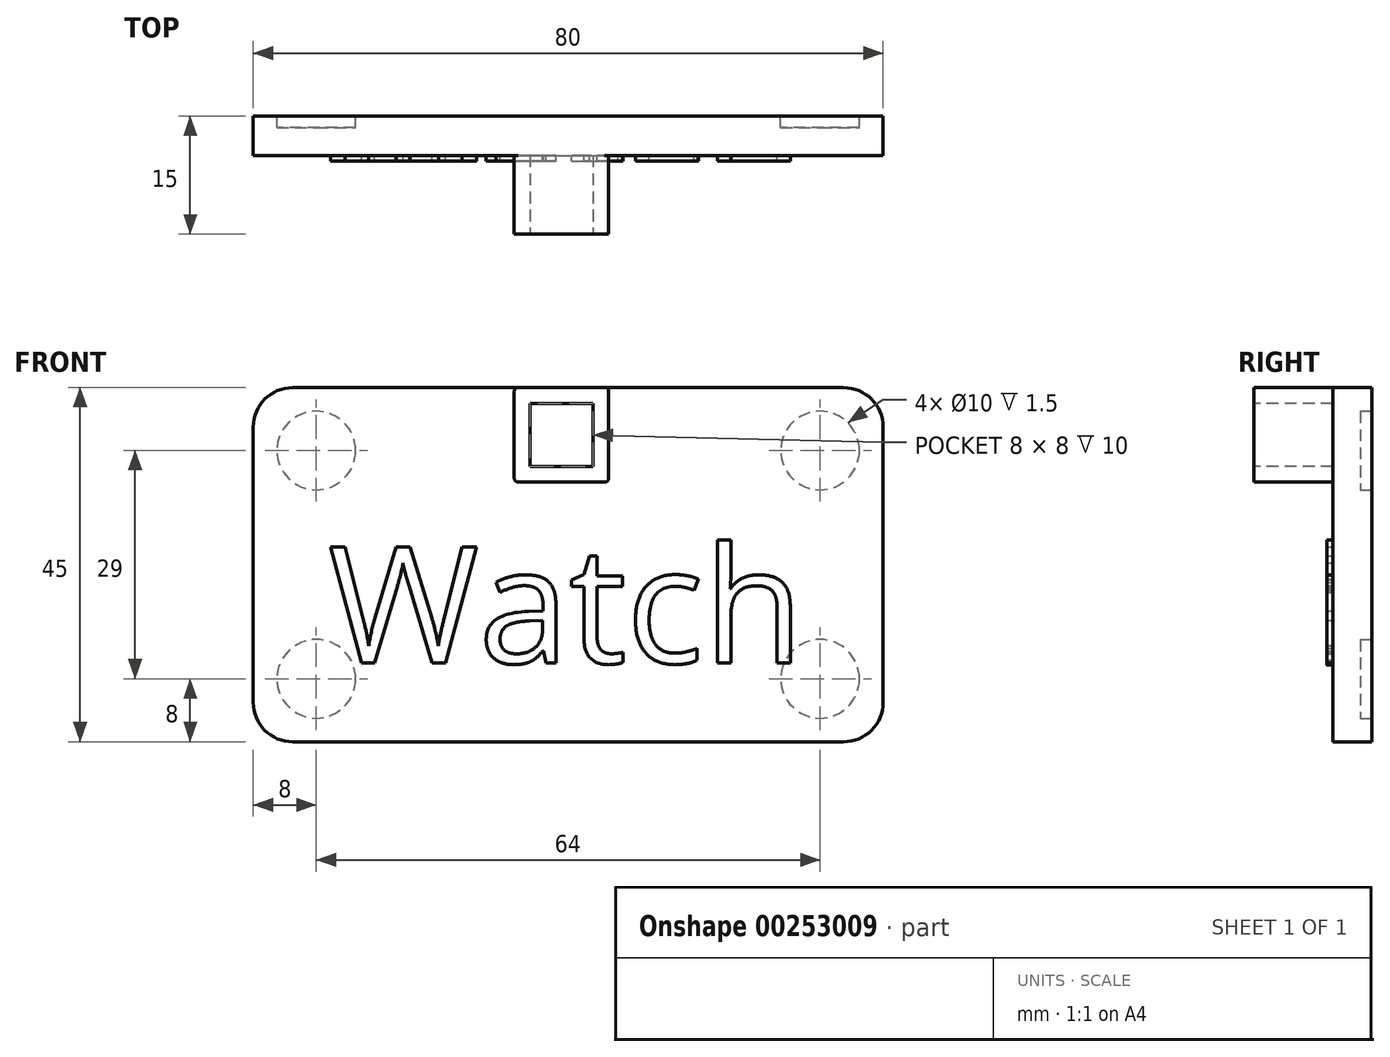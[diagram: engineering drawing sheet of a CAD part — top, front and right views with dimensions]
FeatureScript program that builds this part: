
annotation { "Feature Type Name" : "Feature", "Feature Type Description" : "" }
export const myFeature = defineFeature(function(context is Context, id is Id, definition is map)
    precondition{}
    {
        {
            var Q0;
            Q0=qCreatedBy(makeId("Front.planeOp"),FACE);
            var sketch = newSketch(context, id + "F0", { "sketchPlane" : qUnion([Q0])});
            skLineSegment(sketch, "E0.bottom", {"start": v(-40, 22.5) * mm, "end": v(40, 22.5) * mm});
            skLineSegment(sketch, "E0.top", {"start": v(-40, -22.5) * mm, "end": v(40, -22.5) * mm});
            skLineSegment(sketch, "E0.left", {"start": v(-40, 22.5) * mm, "end": v(-40, -22.5) * mm});
            skLineSegment(sketch, "E0.right", {"start": v(40, 22.5) * mm, "end": v(40, -22.5) * mm});
            skPoint(sketch, "E0.middle", {"position": v(0, 0) * mm});
            skSolve(sketch);
        }
        {
            var Q0;
            Q0 = qSketchRegion(id + "F0", true);
            extrude(context, id + "F1", {"entities" : qUnion([Q0]), "depth" : 5 * mm});
        }
        {
            var Q0;
            Q0=makeQuery(id+"F1.opExtrude","SWEPT_EDGE",EDGE,{"disambiguationData":[OSD([sQuery(id+"F0.wireOp",EDGE,"E0.bottom"),sQuery(id+"F0.wireOp",EDGE,"E0.right")])]});
            var Q1;
            Q1=makeQuery(id+"F1.opExtrude","SWEPT_EDGE",EDGE,{"disambiguationData":[OSD([sQuery(id+"F0.wireOp",EDGE,"E0.top"),sQuery(id+"F0.wireOp",EDGE,"E0.right")])]});
            var Q2;
            Q2=makeQuery(id+"F1.opExtrude","SWEPT_EDGE",EDGE,{"disambiguationData":[OSD([sQuery(id+"F0.wireOp",EDGE,"E0.top"),sQuery(id+"F0.wireOp",EDGE,"E0.left")])]});
            var Q3;
            Q3=makeQuery(id+"F1.opExtrude","SWEPT_EDGE",EDGE,{"disambiguationData":[OSD([sQuery(id+"F0.wireOp",EDGE,"E0.bottom"),sQuery(id+"F0.wireOp",EDGE,"E0.left")])]});
            fillet(context, id + "F2", {"entities" : qUnion([Q0, Q1, Q2, Q3]), "radius" : 5 * mm, "tangentPropagation" : true, "allowEdgeOverflow" : false});
        }
        {
            var Q0;
            Q0=makeQuery(id+"F1.opExtrude","CAP_FACE",FACE,{"disambiguationData":[OSD([sQuery(id+"F0.wireOp",EDGE,"E0.bottom"),sQuery(id+"F0.wireOp",EDGE,"E0.top"),sQuery(id+"F0.wireOp",EDGE,"E0.left"),sQuery(id+"F0.wireOp",EDGE,"E0.right")])],"isStart":false});
            var sketch = newSketch(context, id + "F3", { "sketchPlane" : qUnion([Q0])});
            skLineSegment(sketch, "E1.bottom", {"start": v(-6.85, 22.5) * mm, "end": v(5.15, 22.5) * mm});
            skLineSegment(sketch, "E1.top", {"start": v(-6.85, 10.5) * mm, "end": v(5.15, 10.5) * mm});
            skLineSegment(sketch, "E1.left", {"start": v(-6.85, 22.5) * mm, "end": v(-6.85, 10.5) * mm});
            skLineSegment(sketch, "E1.right", {"start": v(5.15, 22.5) * mm, "end": v(5.15, 10.5) * mm});
            skSolve(sketch);
        }
        {
            var Q0;
            Q0 = qSketchRegion(id + "F3", true);
            extrude(context, id + "F4", {"entities" : qUnion([Q0]), "operationType" : NewBodyOperationType.ADD, "depth" : 10 * mm});
        }
        {
            var Q0;
            Q0=makeQuery(id+"F4.opExtrude","CAP_FACE",FACE,{"disambiguationData":[OSD([sQuery(id+"F3.wireOp",EDGE,"E1.bottom"),sQuery(id+"F3.wireOp",EDGE,"E1.top"),sQuery(id+"F3.wireOp",EDGE,"E1.left"),sQuery(id+"F3.wireOp",EDGE,"E1.right")])],"isStart":false});
            var sketch = newSketch(context, id + "F5", { "sketchPlane" : qUnion([Q0])});
            skLineSegment(sketch, "E2.bottom", {"start": v(-4.85, 20.5) * mm, "end": v(3.15, 20.5) * mm});
            skLineSegment(sketch, "E2.top", {"start": v(-4.85, 12.5) * mm, "end": v(3.15, 12.5) * mm});
            skLineSegment(sketch, "E2.left", {"start": v(-4.85, 20.5) * mm, "end": v(-4.85, 12.5) * mm});
            skLineSegment(sketch, "E2.right", {"start": v(3.15, 20.5) * mm, "end": v(3.15, 12.5) * mm});
            skSolve(sketch);
        }
        {
            var Q0;
            Q0 = qSketchRegion(id + "F5", true);
            extrude(context, id + "F6", {"entities" : qUnion([Q0]), "operationType" : NewBodyOperationType.REMOVE, "oppositeDirection" : true, "depth" : 10 * mm});
        }
        {
            var Q0;
            Q0=makeQuery(id+"F4.opExtrude","SWEPT_EDGE",EDGE,{"disambiguationData":[OSD([sQuery(id+"F3.wireOp",EDGE,"E1.top"),sQuery(id+"F3.wireOp",EDGE,"E1.right")])]});
            var Q1;
            Q1=makeQuery(id+"F4.opExtrude","SWEPT_EDGE",EDGE,{"disambiguationData":[OSD([sQuery(id+"F3.wireOp",EDGE,"E1.top"),sQuery(id+"F3.wireOp",EDGE,"E1.left")])]});
            var Q2;
            Q2=makeQuery(id+"F4.opExtrude","SWEPT_EDGE",EDGE,{"disambiguationData":[OSD([sQuery(id+"F0.wireOp",EDGE,"E0.bottom"),sQuery(id+"F3.wireOp",EDGE,"E1.bottom"),sQuery(id+"F3.wireOp",EDGE,"E1.left")])]});
            var Q3;
            Q3=makeQuery(id+"F4.opExtrude","SWEPT_EDGE",EDGE,{"disambiguationData":[OSD([sQuery(id+"F0.wireOp",EDGE,"E0.bottom"),sQuery(id+"F3.wireOp",EDGE,"E1.bottom"),sQuery(id+"F3.wireOp",EDGE,"E1.right")])]});
            fillet(context, id + "F7", {"entities" : qUnion([Q0, Q1, Q2, Q3]), "radius" : 0.5 * mm, "tangentPropagation" : true, "allowEdgeOverflow" : false});
        }
        {
            var Q0;
            Q0=makeQuery(id+"F1.opExtrude","CAP_FACE",FACE,{"disambiguationData":[OSD([sQuery(id+"F0.wireOp",EDGE,"E0.bottom"),sQuery(id+"F0.wireOp",EDGE,"E0.top"),sQuery(id+"F0.wireOp",EDGE,"E0.left"),sQuery(id+"F0.wireOp",EDGE,"E0.right")])],"isStart":false});
            var sketch = newSketch(context, id + "F8", { "sketchPlane" : qUnion([Q0])});
            skText(sketch, "E3", { "text": "Watch", "fontName": "OpenSans-Regular.ttf"});
            const initialGuessF8  = {"E3": [-0.03045, -0.0125, 1, 0, 0.01485]};
            skSetInitialGuess(sketch, initialGuessF8);
            skSolve(sketch);
        }
        {
            var Q0;
            Q0 = qSketchRegion(id + "F8", true);
            extrude(context, id + "F9", {"entities" : qUnion([Q0]), "operationType" : NewBodyOperationType.ADD, "depth" : 0.75 * mm});
        }
        {
            var Q0;
            Q0=makeQuery(id+"F1.opExtrude","CAP_FACE",FACE,{"disambiguationData":[OSD([sQuery(id+"F0.wireOp",EDGE,"E0.bottom"),sQuery(id+"F0.wireOp",EDGE,"E0.top"),sQuery(id+"F0.wireOp",EDGE,"E0.left"),sQuery(id+"F0.wireOp",EDGE,"E0.right")])],"isStart":true});
            var sketch = newSketch(context, id + "F10", { "sketchPlane" : qUnion([Q0])});
            skCircle(sketch, "E4", {"center": v(-32, 14.5) * mm, "radius": 5 * mm});
            skCircle(sketch, "E5", {"center": v(32, 14.5) * mm, "radius": 5 * mm});
            skCircle(sketch, "E6", {"center": v(32, -14.5) * mm, "radius": 5 * mm});
            skCircle(sketch, "E7", {"center": v(-32, -14.5) * mm, "radius": 5 * mm});
            skSolve(sketch);
        }
        {
            var Q0;
            Q0 = qSketchRegion(id + "F10", true);
            extrude(context, id + "F11", {"entities" : qUnion([Q0]), "operationType" : NewBodyOperationType.REMOVE, "oppositeDirection" : true, "depth" : 1.5 * mm});
        }
    });
